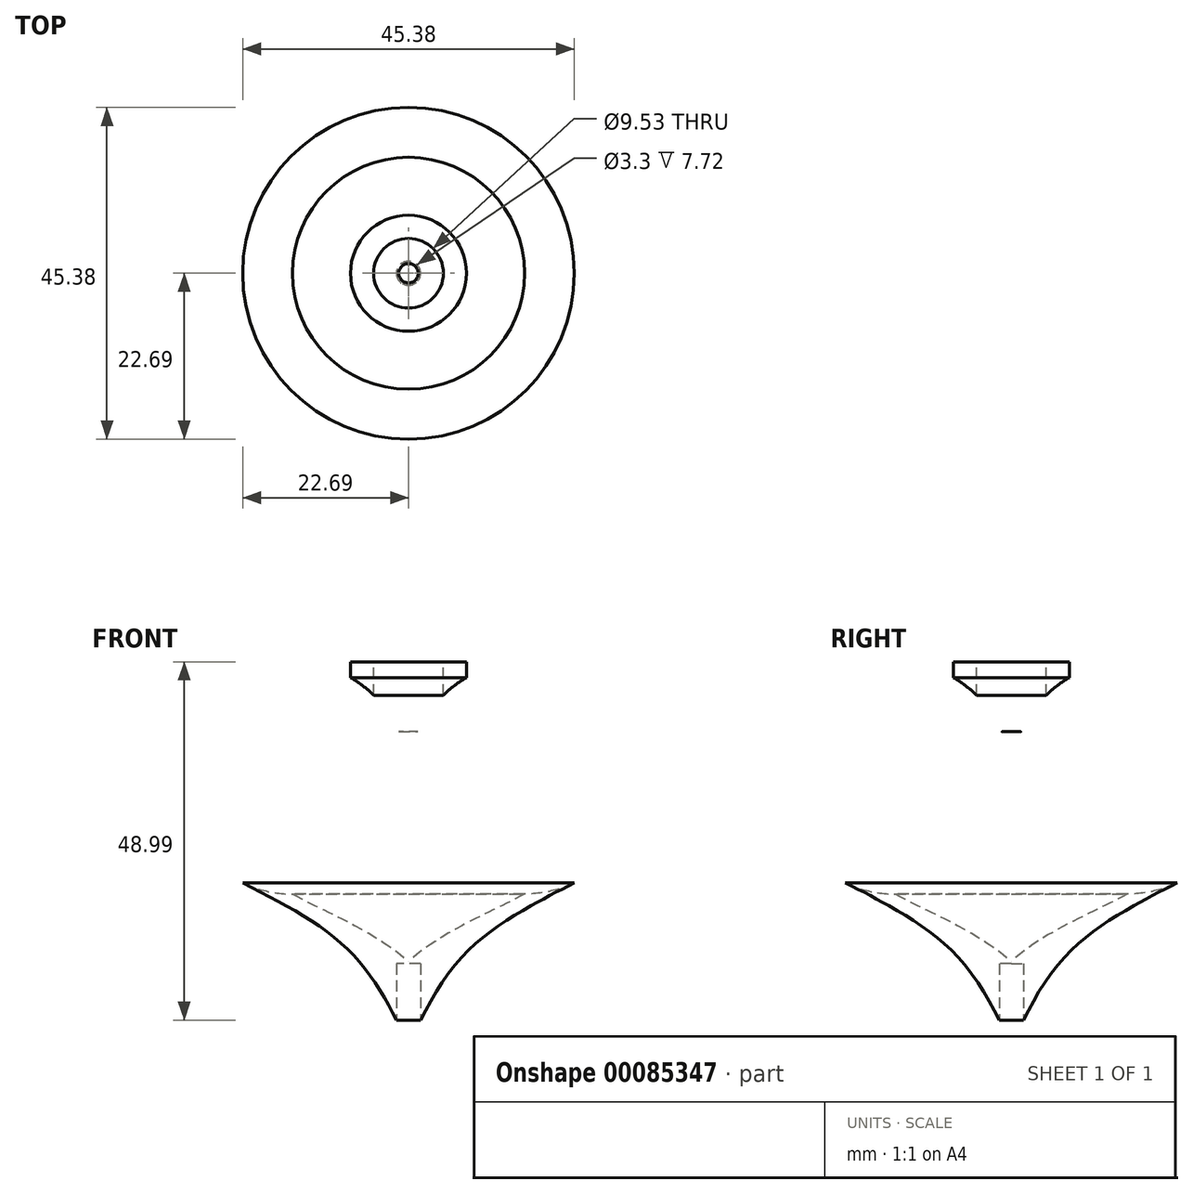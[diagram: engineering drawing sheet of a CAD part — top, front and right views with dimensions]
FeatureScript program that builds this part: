
annotation { "Feature Type Name" : "Feature", "Feature Type Description" : "" }
export const myFeature = defineFeature(function(context is Context, id is Id, definition is map)
    precondition{}
    {
        {
            var Q0;
            Q0=qCreatedBy(makeId("Right.planeOp"),FACE);
            var sketch = newSketch(context, id + "F0", { "sketchPlane" : qUnion([Q0])});
            skFitSpline(sketch, "E0", {"points": [v(0, 11.11) * mm, v(7.94, 23.81) * mm, v(23.43, 33.66) * mm], "startDerivative": vector(13.7, 28.66) * mm, "endDerivative": vector(32.82, 16.67) * mm});
            skArc(sketch, "E1", {"start": v(15.87, 63.5) * mm, "mid": v(31.26, 51.52) * mm, "end": v(23.43, 33.66) * mm});
            skLineSegment(sketch, "E2", {"start": v(0, 11.11) * mm, "end": v(0, 0) * mm});
            skCircle(sketch, "E3", {"center": v(15.87, 47.62) * mm, "radius": 15.88 * mm});
            skLineSegment(sketch, "E4", {"start": v(7.94, 63.5) * mm, "end": v(7.94, 61.37) * mm});
            skFitSpline(sketch, "E5", {"points": [v(15.87, 31.75) * mm, v(7.13, 27.34) * mm, v(0, 22.54) * mm], "startDerivative": vector(-18.68, -9.92) * mm, "endDerivative": vector(-12.95, -11.64) * mm});
            skLineSegment(sketch, "E6", {"start": v(0, 63.5) * mm, "end": v(7.94, 63.5) * mm});
            skLineSegment(sketch, "E7", {"start": v(0, 11.11) * mm, "end": v(0, 22.54) * mm});
            skLineSegment(sketch, "E8", {"start": v(0, 63.5) * mm, "end": v(0, 47.62) * mm});
            skSolve(sketch);
        }
        {
            var Q0;
            Q0=makeQuery(id+"F0.imprint","IMPRINT",FACE,{"disambiguationData":[TD([[makeQuery(id+"F0.imprint","IMPRINT",EDGE,{"derivedFrom":sQuery(id+"F0.wireOp",EDGE,"E0")}),1.0]])]});
            var Q1;
            {var subQ0=sQuery(id+"F0.wireOp",EDGE,"E3");var subQ2=sQuery(id+"F0.wireOp",EDGE,"E0");var subQ6=makeQuery(id+"F0.imprint","INTERSECT",VERTEX,{"disambiguationData":[OD(0.0)],"derivedFrom":[subQ2,subQ0]});Q1=makeQuery(id+"F0.imprint","IMPRINT",FACE,{"disambiguationData":[TD([[makeQuery(id+"F0.imprint","IMPRINT",EDGE,{"disambiguationData":[TD([[subQ6,1.0]])],"derivedFrom":subQ2}),1.0]])]});}
            var Q2;
            {var subQ0=sQuery(id+"F0.wireOp",EDGE,"E4");Q2=makeQuery(id+"F0.imprint","IMPRINT",FACE,{"disambiguationData":[TD([[makeQuery(id+"F0.imprint","IMPRINT",EDGE,{"derivedFrom":subQ0}),-1.0]])]});}
            var Q3;
            Q3=sQuery(id+"F0.wireOp",EDGE,"E7");
            revolve(context, id + "F1", {"entities" : qUnion([Q0, Q1, Q2]), "axis" : qUnion([Q3]), "revolveType" : RevolveType.FULL});
        }
        {
            var Q0;
            Q0=makeQuery(id+"F1.opRevolve","SWEPT_FACE",FACE,{"disambiguationData":[OSD([sQuery(id+"F0.wireOp",EDGE,"E6")])]});
            var sketch = newSketch(context, id + "F2", { "sketchPlane" : qUnion([Q0])});
            skCircle(sketch, "E9", {"center": v(0, 0) * mm, "radius": 4.76 * mm});
            skSolve(sketch);
        }
        {
            var Q0;
            Q0=qSketchRegion(id+"F2",true);
            extrude(context, id + "F3", {"entities" : qUnion([Q0]), "operationType" : NewBodyOperationType.REMOVE, "oppositeDirection" : true, "depth" : 9.52 * mm});
        }
        {
            var Q0;
            Q0=qCreatedBy(makeId("Top.planeOp"),FACE);
            var sketch = newSketch(context, id + "F4", { "sketchPlane" : qUnion([Q0])});
            skCircle(sketch, "E10", {"center": v(0, 0) * mm, "radius": 1.65 * mm});
            skSolve(sketch);
        }
        {
            var Q0;
            Q0=makeQuery(id+"F4.imprint","IMPRINT",FACE,{"disambiguationData":[TD([[makeQuery(id+"F4.imprint","IMPRINT",EDGE,{"derivedFrom":sQuery(id+"F4.wireOp",EDGE,"E10")}),1.0]])]});
            extrude(context, id + "F5", {"entities" : qUnion([Q0]), "operationType" : NewBodyOperationType.REMOVE, "depth" : 22.22 * mm});
        }
    });
